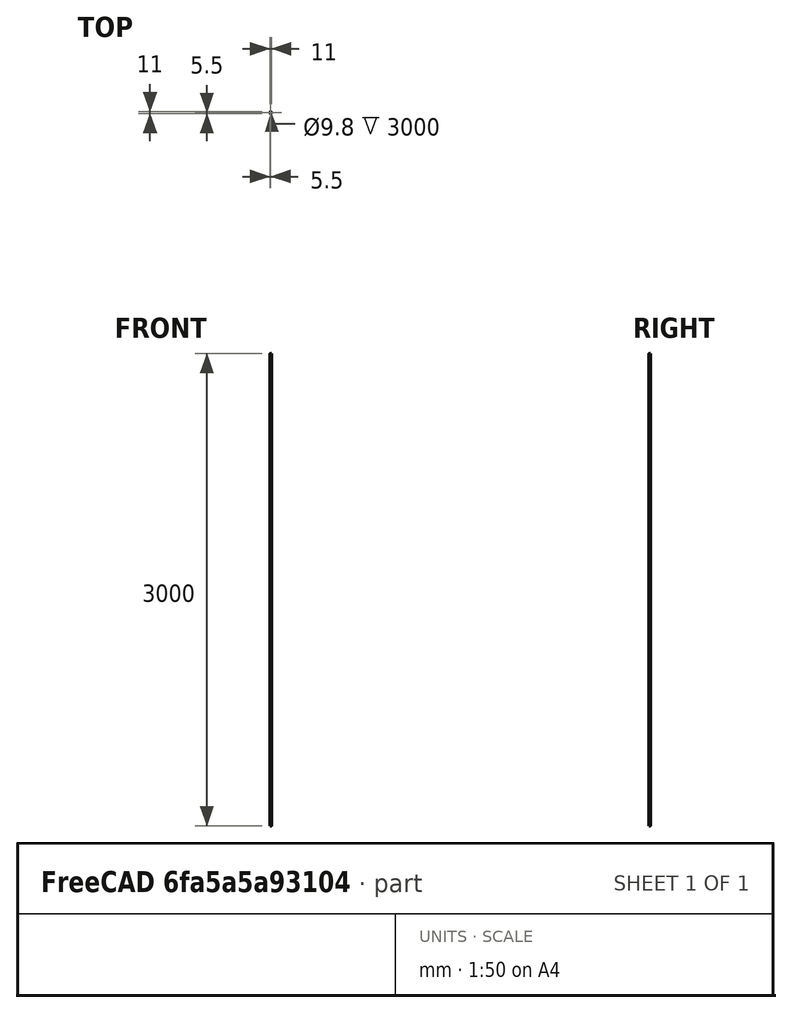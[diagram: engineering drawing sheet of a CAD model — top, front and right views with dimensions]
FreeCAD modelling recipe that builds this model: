
FCSTD DOCUMENT  (FreeCAD 0.21R33771 (Git))
Label: coreGraphic
License: All rights reserved
LicenseURL: http://en.wikipedia.org/wiki/All_rights_reserved
objects: Sketcher::SketchObject×2, PartDesign::Pad×1, PartDesign::Body×1
note: 5 computed .brp shape members not serialized (recipe doc carries the construction recipe); baked Part::Feature solids carry a one-line shape summary decoded from their .brp

FEATURE [Sketcher::SketchObject] Sketch
  FullyConstrained = true
  MapMode = 5
  Support = -> [XY_Plane]
  sketch-geometry (2):
    g0: Circle CenterX=0 CenterY=0 CenterZ=0 NormalX=0 NormalY=0 NormalZ=1 AngleXU=0 Radius=5.5
    g1: Circle CenterX=0 CenterY=0 CenterZ=0 NormalX=0 NormalY=0 NormalZ=1 AngleXU=0 Radius=4.9
  constraints (4):
    c: Coincident(g0,g-1)
    c: Diameter(g0) = 11
    c: Coincident(g1,g0)
    c: Diameter(g1) = 9.8
FEATURE [PartDesign::Pad] Pad
  Direction = (0,0,1)
  Length = 3000
  Length2 = 10
  Profile = -> Sketch
  ReferenceAxis = -> Sketch [N_Axis]
  Type = 0
FEATURE [PartDesign::Body] Body
  Group = -> [Sketch,Pad]
  Origin = -> Origin
  Tip = -> Pad
FEATURE [Sketcher::SketchObject] Sketch001
  FullyConstrained = true
  sketch-geometry (7):
    g0: LineSegment StartX=8.73 StartY=0 StartZ=0 EndX=4.365 EndY=7.5604 EndZ=0
    g1: LineSegment StartX=4.365 StartY=7.5604 StartZ=0 EndX=-4.365 EndY=7.5604 EndZ=0
    g2: LineSegment StartX=-4.365 StartY=7.5604 StartZ=0 EndX=-8.73 EndY=0 EndZ=0
    g3: LineSegment StartX=-8.73 StartY=0 StartZ=0 EndX=-4.365 EndY=-7.5604 EndZ=0
    g4: LineSegment StartX=-4.365 StartY=-7.5604 StartZ=0 EndX=4.365 EndY=-7.5604 EndZ=0
    g5: LineSegment StartX=4.365 StartY=-7.5604 StartZ=0 EndX=8.73 EndY=0 EndZ=0
    g6: Circle CenterX=0 CenterY=0 CenterZ=0 NormalX=0 NormalY=0 NormalZ=1 AngleXU=0 Radius=8.73
  constraints (16):
    c: Coincident(g0,g1)
    c: Coincident(g1,g2)
    c: Coincident(g2,g3)
    c: Coincident(g3,g4)
    c: Coincident(g4,g5)
    c: Coincident(g5,g0)
    c: Equal(g0, g1-g5) x5
    c: PointOnObject(g0,g6)
    c: PointOnObject(g1,g6)
    c: PointOnObject(g2,g6)
    c: PointOnObject(g3,g6)
    c: PointOnObject(g4,g6)
    c: PointOnObject(g5,g6)
    c: Coincident(g6,g-1)
    c: PointOnObject(g5,g-1)
    c: Diameter(g6) = 17.46
